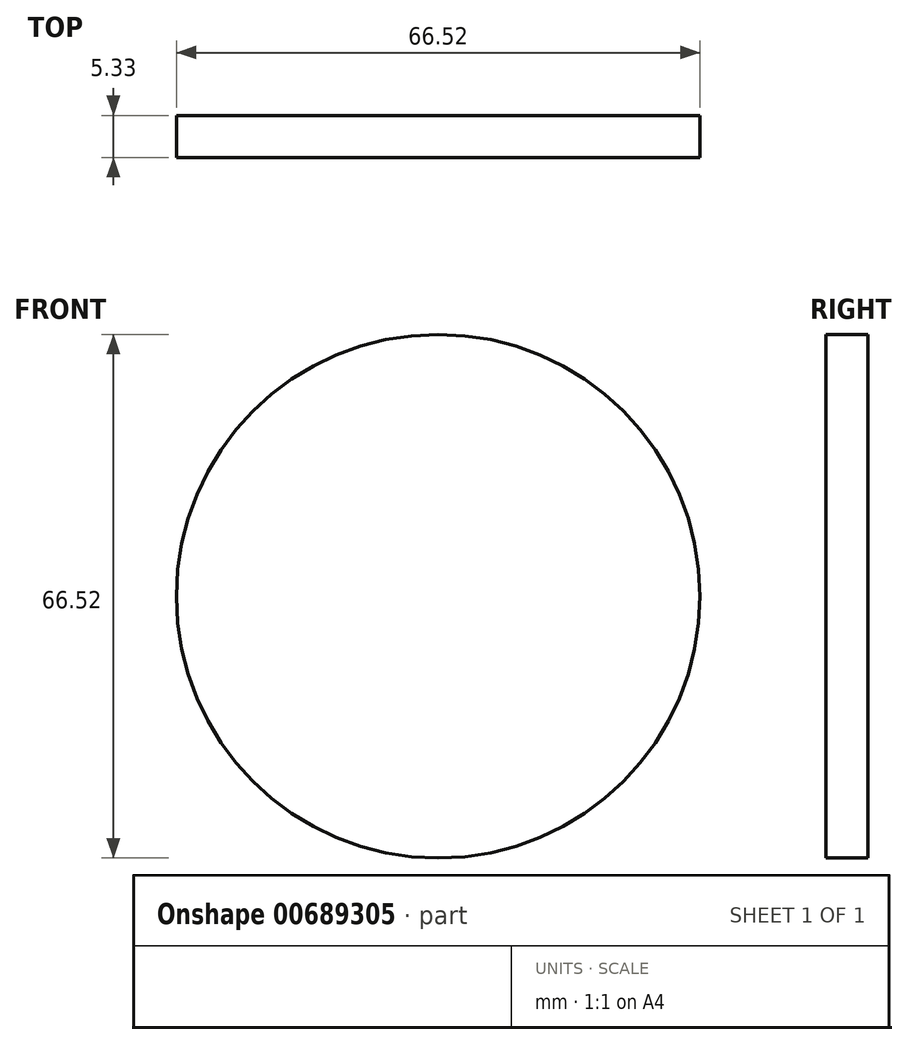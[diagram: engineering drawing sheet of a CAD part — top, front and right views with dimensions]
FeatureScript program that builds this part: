
annotation { "Feature Type Name" : "Feature", "Feature Type Description" : "" }
export const myFeature = defineFeature(function(context is Context, id is Id, definition is map)
    precondition{}
    {
        {
            var Q0;
            Q0=qCreatedBy(makeId("Front.planeOp"),FACE);
            var sketch = newSketch(context, id + "F0", { "sketchPlane" : qUnion([Q0])});
            skCircle(sketch, "E0", {"center": v(0, 0) * mm, "radius": 33.26 * mm});
            skSolve(sketch);
        }
        {
            var Q0;
            Q0=makeQuery(id+"F0.imprint","IMPRINT",FACE,{"disambiguationData":[TD([[makeQuery(id+"F0.imprint","IMPRINT",EDGE,{"derivedFrom":sQuery(id+"F0.wireOp",EDGE,"E0")}),1.0]])]});
            extrude(context, id + "F1", {"entities" : qUnion([Q0]), "depth" : 5.33 * mm, "offsetDistance" : 25.4 * mm});
        }
    });
